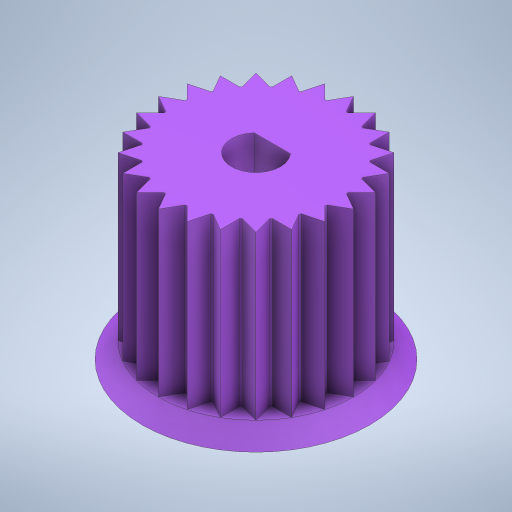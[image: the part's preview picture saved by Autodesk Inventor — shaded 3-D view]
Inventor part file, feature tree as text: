
AUTODESK INVENTOR PART (.ipt)
format: ipt  version: 2023 (Build 270158000, 158)  size: 372,224 bytes
history: mixed  units: in
note: dims shown in document units (in); Inventor stores cm internally (conversion verified against a paired STEP export)
features: other x1, extrude x1, sketch x1, imported_body x1
ambient origin geometry x8: Origin, YZ Plane, XZ Plane, XY Plane, X Axis, Y Axis, Z Axis, Center Point
bodies: Solid1 (imported_parasolid), Body1 (imported_parasolid)
feature tree (4):
  other  "Repaired Geometry1"
  extrude  "Extrusion1"  TaperAngle=0.0deg  [1 undecoded]
  sketch  "Sketch2"  dims[d1=0.0984in d2=0.0in d3=0.0in]
  imported_body  NMx_Import_Brep_tag  [imported B-rep: ~5 faces, bbox_mm=None]
note: 1 required parameter value undecoded (feature->parameter linkage not recoverable at this tier; creation-order binding heuristic only, values carry confidence <= 0.55)
